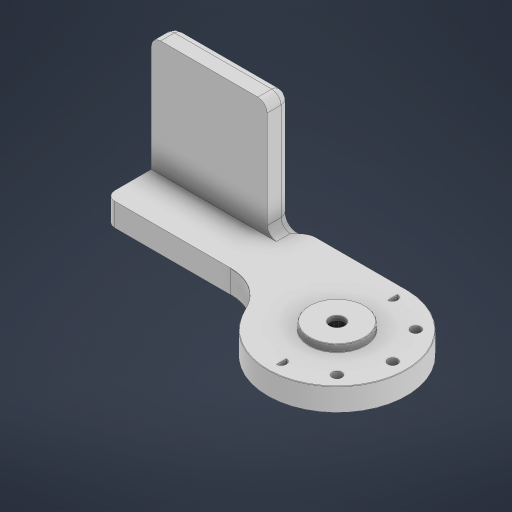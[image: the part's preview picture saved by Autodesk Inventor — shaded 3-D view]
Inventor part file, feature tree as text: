
AUTODESK INVENTOR PART (.ipt)
format: ipt  version: 2023 (Build 270158000, 158)  size: 455,168 bytes
history: native  units: in
note: dims shown in document units (in); Inventor stores cm internally (conversion verified against a paired STEP export)
features: extrude x3, sketch x2, fillet x2, other x1
ambient origin geometry x8: Origin, YZ Plane, XZ Plane, XY Plane, X Axis, Y Axis, Z Axis, Center Point
bodies: Solid1 (feature_tree)
feature tree (8):
  sketch  "Sketch1"  dims[d0=1.9685in d1=1.1732in]
  extrude  "Extrusion1"  Depth=1.1732in
  extrude  "Extrusion2"  Depth=0.0787in TaperAngle=0.0deg
  fillet  "Fillet1"  Radius=0.3937in
  extrude  "Extrusion3"  Depth=0.0787in
  fillet  "Fillet2"  Radius=0.1969in
  sketch  "Sketch2"  dims[d2=0.3937in d3=0.0in d4=0.1969in d5=0.0in d6=0.3937in d7=0.9843in d8=0.1969in d9=0.9843in d10=0.0in d11=0.0787in]
  other  "Répétition circulaire3"
